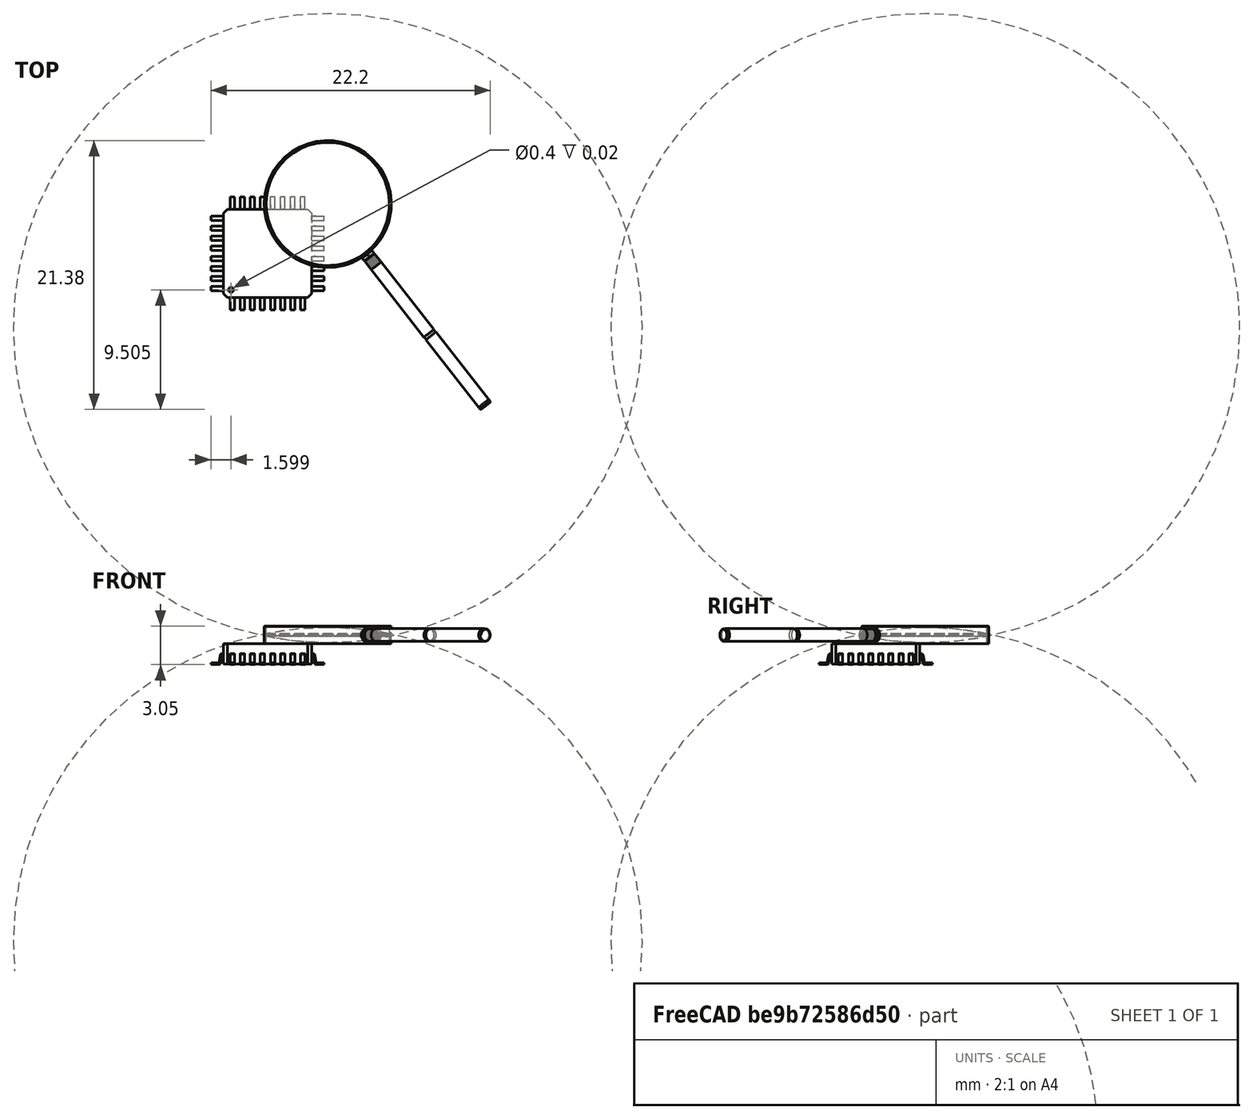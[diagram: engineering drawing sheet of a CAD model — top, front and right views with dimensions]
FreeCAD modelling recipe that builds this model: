
FCSTD DOCUMENT  (FreeCAD 0.16R6703 (Git))
Label: fpga-config
License: CC-BY 3.0
LicenseURL: http://creativecommons.org/licenses/by/3.0/
objects: Part::Feature×3, Part::Compound×2, Part::FeaturePython×1
note: 6 computed .brp shape members not serialized (recipe doc carries the construction recipe); baked Part::Feature solids carry a one-line shape summary decoded from their .brp

FEATURE [Part::Compound] Compound020  label="PQFP-034"
  Placement = pos=(-5.71099,-9.13488,1.7) rot=(0,0,1;0rad)
FEATURE [Part::Feature] Part__Feature  label="100mm Magnifying Glass"
  shape: bbox 108 x 11.7 x 108 mm, 14 faces (baked)
FEATURE [Part::Feature] Part__Feature001  label="100mm Magnifying Glass001"
  shape: bbox 113.6 x 14 x 101 mm, 77 faces (baked)
FEATURE [Part::Feature] Part__Feature002  label="100mm Magnifying Glass002"
  shape: bbox 150.3 x 11.24 x 11.24 mm, 25 faces (baked)
FEATURE [Part::Compound] Compound  label="mag-glass-orig"
  Links = -> [Part__Feature,Part__Feature001,Part__Feature002]
  Placement = pos=(0,0,0) rot=(1,0,0;1.5708rad)
FEATURE [Part::FeaturePython] Clone  label="mag-glass"  # Draft clone (typed FeaturePython)
  Objects = -> [Compound]
  Placement = pos=(3.59914,-0.709704,4) rot=(0.823173,-0.401489,-0.401489;1.76417rad)
  Scale = (0.1,0.1,0.1)
